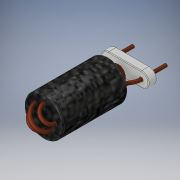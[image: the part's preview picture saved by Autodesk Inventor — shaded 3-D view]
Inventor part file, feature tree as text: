
AUTODESK INVENTOR PART (.ipt)
format: ipt  version: 2019.1 (Build 231200000, 200)  size: 369,664 bytes
history: native  units: in
note: dims shown in document units (in); Inventor stores cm internally (conversion verified against a paired STEP export)
features: sketch x7, extrude x6, sweep x2, revolve x2, fillet x2, thicken_offset x2, hole x1, plane x1
ambient origin geometry x8: Origin, YZ Plane, XZ Plane, XY Plane, X Axis, Y Axis, Z Axis, Center Point
bodies: Solid1 (feature_tree), Solid2 (feature_tree), Solid3 (feature_tree)
feature tree (23):
  sketch  "Sketch1"  dims[d0=0.09in d1=0.09in]
  extrude  "Extrusion1"  Depth=0.09in
  hole  "Hole1"  [1 undecoded]
  extrude  "Extrusion2"  Depth=0.02in
  extrude  "Extrusion3"  Depth=0.05in TaperAngle=0.0deg
  plane  "Work Plane1"
  extrude  "Extrusion4"  Depth=0.1in
  sketch  "Sketch3"  dims[d4=0.02in d5=0.02in]
  sketch  "Sketch4"  dims[d6=0.05in d7=0.0in]
  sweep  "Sweep1"
  sweep  "Sweep2"
  extrude  "Extrusion5"  Depth=0.0039in
  sketch  "Sketch6"  dims[d17=0.2in d18=0.0in d19=0.1in]
  revolve  "Revolution1"  [1 undecoded]
  extrude  "Extrusion6"  Depth=0.0039in
  revolve  "Revolution2"  [1 undecoded]
  fillet  "Fillet1"  [1 undecoded]
  fillet  "Fillet2"  Radius=0.025in
  thicken_offset  "Thicken1"
  thicken_offset  "Thicken2"
  sketch  "Sketch2"  dims[d2=0.0in d3=0.2in]
  sketch  "Sketch5"  dims[d8=0.025in d9=0.2362in d10=0.1575in d11=0.0787in d12=90.0deg d13=0.315in d14=0.0in d15=0.05in d16=0.0in]
  sketch  "Sketch7"  dims[d20=0.2362in d21=0.3937in d22=0.0in d24=0.0in d26=0.069in d27=0.025in d29=0.025in d30=0.069in d31=225.0deg d36=0.025in d37=0.069in d38=0.7874in d40=360.0deg d42=0.1in d43=0.1in d44=0.1in d45=0.1in d46=0.0in d47=0.0in d48=0.0in d49=0.0in d50=0.3937in d51=0.0in d52=0.02in d53=0.02in d54=0.1181in d55=45.0deg d56=180.0deg d57=0.02in d58=0.02in d59=0.02in d60=0.02in d61=0.02in d62=0.02in d63=0.3937in d64=0.0in d65=180.0deg d66=0.0079in d67=0.0039in d68=0.1in d69=0.1in d70=0.1in d71=0.1in]
note: 4 required parameter values undecoded (feature->parameter linkage not recoverable at this tier; creation-order binding heuristic only, values carry confidence <= 0.55)